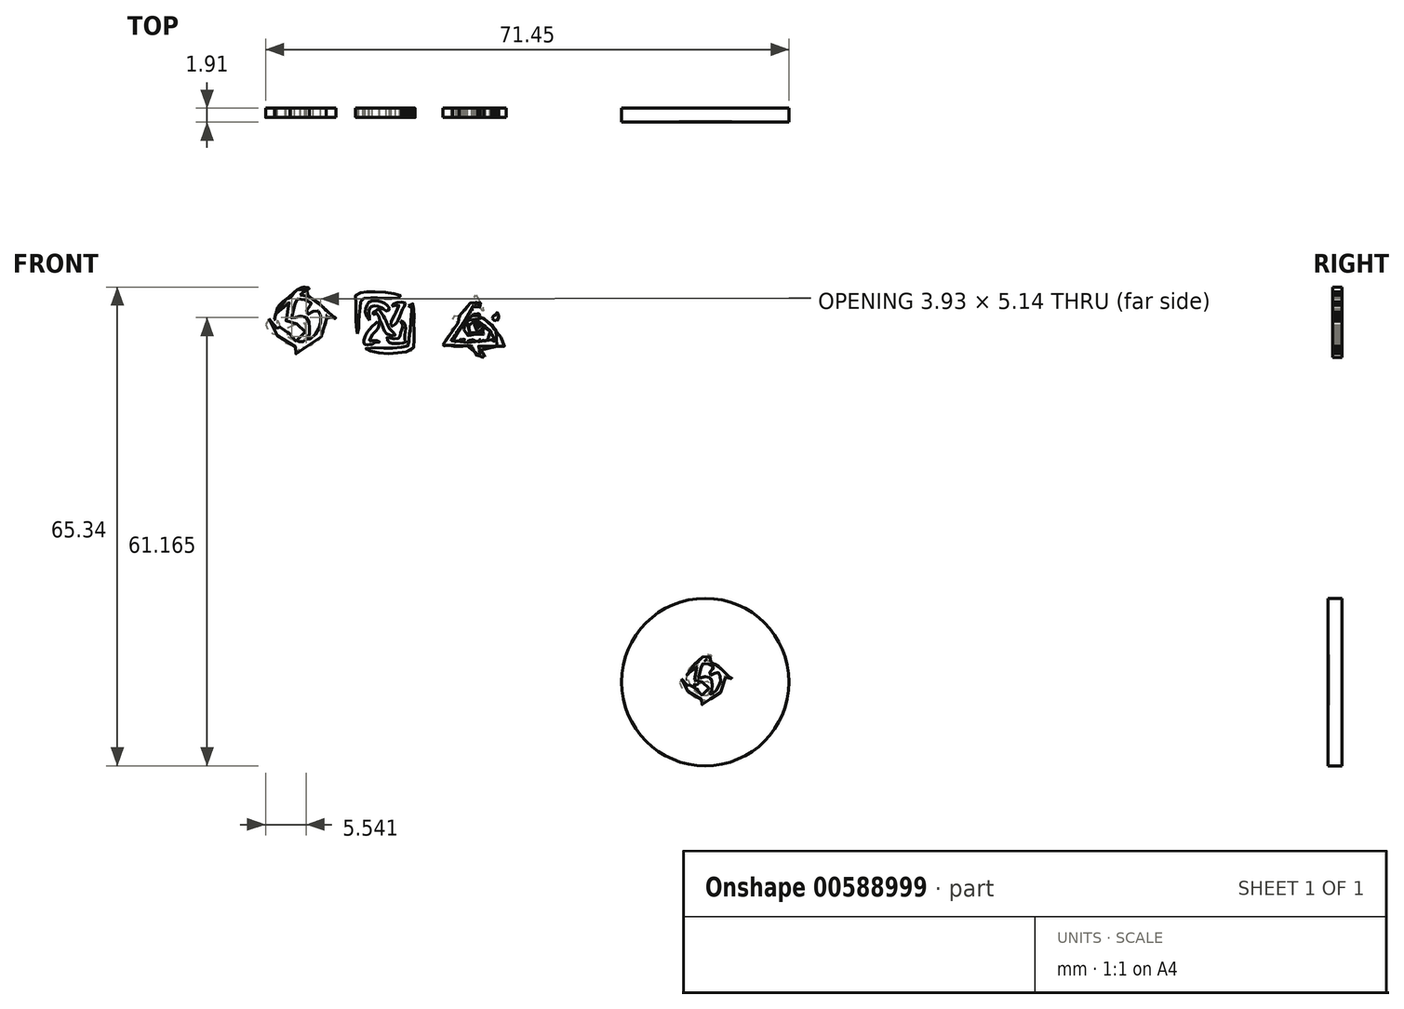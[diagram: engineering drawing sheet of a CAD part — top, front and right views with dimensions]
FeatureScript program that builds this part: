
annotation { "Feature Type Name" : "Feature", "Feature Type Description" : "" }
export const myFeature = defineFeature(function(context is Context, id is Id, definition is map)
    precondition{}
    {
        {
            var Q0;
            Q0=qCreatedBy(makeId("Front.planeOp"),FACE);
            var sketch = newSketch(context, id + "F0", { "sketchPlane" : qUnion([Q0])});
            skCircle(sketch, "E0", {"center": v(0, 0) * mm, "radius": 11.43 * mm});
            skSolve(sketch);
        }
        {
            var Q0;
            Q0=qSketchRegion(id+"F0",true);
            extrude(context, id + "F1", {"entities" : qUnion([Q0]), "depth" : 1.9 * mm, "offsetDistance" : 25.4 * mm});
        }
        {
            var Q0;
            Q0=makeQuery(id+"F1.opExtrude","CAP_FACE",FACE,{"disambiguationData":[OSD([sQuery(id+"F0.wireOp",EDGE,"E0")])],"isStart":false});
            var sketch = newSketch(context, id + "F2", { "sketchPlane" : qUnion([Q0])});
            skFitSpline(sketch, "E1", {"points": [v(-3.24, 0.45) * mm, v(-3.55, 0.04) * mm, v(-3.49, -0.19) * mm, v(-3.34, -0.6) * mm, v(-3.02, -0.9) * mm, v(-2.64, -1.13) * mm, v(-2.34, -1.25) * mm, v(-2.3, -1.13) * mm, v(-2.1, -1.5) * mm, v(-1.73, -1.77) * mm, v(-1.3, -2.12) * mm, v(-0.73, -2.32) * mm, v(-0.3, -2.43) * mm, v(0.02, -2.42) * mm, v(-0.07, -2.54) * mm, v(-0.16, -2.68) * mm, v(-0.32, -2.86) * mm, v(-0.45, -2.97) * mm, v(-0.58, -3.05) * mm, v(-0.6, -3.15) * mm, v(-0.45, -3.1) * mm, v(-0.28, -3.04) * mm, v(-0.18, -3) * mm, v(-0.02, -2.86) * mm, v(0.1, -2.77) * mm, v(0.18, -2.65) * mm, v(0.23, -2.56) * mm, v(0.3, -2.5) * mm, v(0.33, -2.4) * mm, v(0.53, -2.37) * mm, v(0.74, -2.32) * mm, v(0.97, -2.25) * mm, v(1.17, -2.16) * mm, v(1.39, -2) * mm, v(1.54, -1.9) * mm, v(1.75, -1.8) * mm, v(1.9, -1.64) * mm, v(2.05, -1.47) * mm, v(2.2, -1.23) * mm, v(2.35, -0.98) * mm, v(2.46, -0.8) * mm, v(2.57, -0.46) * mm, v(2.66, -0.14) * mm, v(2.72, 0.23) * mm, v(2.7, 0.55) * mm, v(2.65, 0.84) * mm, v(2.79, 0.76) * mm, v(2.98, 0.66) * mm, v(3.23, 0.55) * mm, v(3.44, 0.51) * mm, v(3.58, 0.52) * mm, v(3.6, 0.57) * mm, v(3.4, 0.67) * mm, v(3.26, 0.77) * mm, v(3.16, 0.89) * mm, v(3, 1) * mm, v(2.86, 1.12) * mm, v(2.76, 1.23) * mm, v(2.57, 1.37) * mm, v(2.48, 1.47) * mm, v(2.38, 1.63) * mm, v(2.21, 1.74) * mm, v(2.07, 1.9) * mm, v(1.87, 2.07) * mm, v(1.76, 2.2) * mm, v(1.56, 2.33) * mm, v(1.4, 2.41) * mm, v(1.15, 2.53) * mm, v(0.96, 2.72) * mm, v(0.66, 2.81) * mm, v(0.46, 2.81) * mm, v(0.16, 2.91) * mm, v(-0.02, 2.89) * mm, v(0.08, 3) * mm, v(0.16, 3.1) * mm, v(0.28, 3.18) * mm, v(0.5, 3.3) * mm, v(0.64, 3.4) * mm, v(0.84, 3.51) * mm, v(0.9, 3.6) * mm, v(0.62, 3.66) * mm, v(0.43, 3.7) * mm, v(0.26, 3.7) * mm, v(0.1, 3.65) * mm, v(-0.02, 3.59) * mm, v(-0.19, 3.52) * mm, v(-0.37, 3.38) * mm, v(-0.53, 3.25) * mm, v(-0.65, 3.12) * mm, v(-0.76, 2.97) * mm, v(-0.81, 2.87) * mm, v(-0.93, 2.7) * mm, v(-1.18, 2.6) * mm, v(-1.34, 2.52) * mm, v(-1.47, 2.45) * mm, v(-1.69, 2.3) * mm, v(-1.88, 2.16) * mm, v(-2.1, 1.93) * mm, v(-2.25, 1.75) * mm, v(-2.35, 1.5) * mm, v(-2.46, 1.26) * mm, v(-2.5, 1.02) * mm, v(-2.6, 0.77) * mm, v(-2.61, 0.53) * mm, v(-2.62, 0.36) * mm, v(-2.56, 0.33) * mm, v(-2.54, 0.55) * mm, v(-2.5, 0.7) * mm, v(-2.4, 0.9) * mm, v(-2.28, 1.15) * mm, v(-2.16, 1.33) * mm, v(-2.01, 1.56) * mm, v(-1.84, 1.8) * mm, v(-1.69, 1.92) * mm, v(-1.5, 2.05) * mm, v(-1.25, 2.22) * mm, v(-1.09, 2.31) * mm, v(-1.16, 2.12) * mm, v(-1.27, 1.86) * mm, v(-1.3, 1.73) * mm, v(-1.37, 1.39) * mm, v(-1.39, 1.23) * mm, v(-1.42, 0.93) * mm, v(-1.43, 0.69) * mm, v(-1.44, 0.4) * mm, v(-1.47, 0.07) * mm, v(-1.44, -0.2) * mm, v(-1.42, -0.5) * mm, v(-1.15, -0.34) * mm, v(-0.97, -0.26) * mm, v(-0.72, -0.18) * mm, v(-0.47, -0.08) * mm, v(-0.2, 0) * mm, v(0.1, 0.1) * mm, v(0.25, 0.13) * mm, v(0.38, 0.08) * mm, v(0.48, -0.18) * mm, v(0.48, -0.4) * mm, v(0.5, -0.6) * mm, v(0.5, -0.8) * mm, v(0.47, -1) * mm, v(0.46, -1.29) * mm, v(0.38, -1.62) * mm, v(0.33, -1.82) * mm, v(0.18, -1.88) * mm, v(-0.02, -1.87) * mm, v(-0.25, -1.83) * mm, v(-0.47, -1.8) * mm, v(-0.7, -1.75) * mm, v(-0.85, -1.65) * mm, v(-1.06, -1.52) * mm, v(-1.22, -1.44) * mm, v(-1.4, -1.3) * mm, v(-1.57, -1.1) * mm, v(-1.3, -1.1) * mm, v(-1.07, -1.05) * mm, v(-0.97, -1.04) * mm, v(-1.12, -0.92) * mm, v(-1.24, -0.85) * mm, v(-1.42, -0.8) * mm, v(-1.59, -0.77) * mm, v(-1.77, -0.74) * mm, v(-1.86, -0.74) * mm, v(-2, -0.53) * mm, v(-2.1, -0.3) * mm, v(-2.13, -0.1) * mm, v(-2.21, 0.12) * mm, v(-2.3, 0.26) * mm, v(-2.38, 0.33) * mm, v(-2.38, 0.06) * mm, v(-2.4, -0.06) * mm, v(-2.42, -0.25) * mm, v(-2.42, -0.4) * mm, v(-2.42, -0.59) * mm, v(-2.56, -0.53) * mm, v(-2.67, -0.42) * mm, v(-2.83, -0.27) * mm, v(-2.86, -0.14) * mm, v(-2.93, 0.09) * mm, v(-2.98, 0.3) * mm, v(-3.1, 0.43) * mm, v(-3.24, 0.45) * mm]});
            skFitSpline(sketch, "E2", {"points": [v(-0.32, 2.52) * mm, v(0.04, 2.5) * mm, v(0.43, 2.43) * mm, v(0.8, 2.33) * mm, v(1, 2.17) * mm, v(1.28, 1.96) * mm, v(1.13, 1.9) * mm, v(0.97, 1.78) * mm, v(0.78, 1.64) * mm, v(0.62, 1.46) * mm, v(0.62, 1.25) * mm, v(0.64, 1.08) * mm, v(0.63, 0.94) * mm, v(0.89, 0.97) * mm, v(1.04, 1.1) * mm, v(1.19, 1.16) * mm, v(1.37, 1.27) * mm, v(1.55, 1.3) * mm, v(1.72, 1.3) * mm, v(1.87, 1.25) * mm, v(1.97, 1.06) * mm, v(2.04, 0.88) * mm, v(2.06, 0.6) * mm, v(2.07, 0.2) * mm, v(2.07, -0.04) * mm, v(1.97, -0.28) * mm, v(1.84, -0.58) * mm, v(1.78, -0.8) * mm, v(1.63, -0.98) * mm, v(1.46, -1.2) * mm, v(1.24, -1.4) * mm, v(0.95, -1.6) * mm, v(0.72, -1.72) * mm, v(0.63, -1.74) * mm, v(0.74, -1.55) * mm, v(0.82, -1.35) * mm, v(0.9, -1.15) * mm, v(0.9, -0.89) * mm, v(0.93, -0.62) * mm, v(0.93, -0.38) * mm, v(0.91, -0.17) * mm, v(0.91, 0.04) * mm, v(0.87, 0.24) * mm, v(0.78, 0.41) * mm, v(0.62, 0.58) * mm, v(0.42, 0.7) * mm, v(0.26, 0.7) * mm, v(0.04, 0.74) * mm, v(-0.1, 0.7) * mm, v(-0.33, 0.66) * mm, v(-0.53, 0.59) * mm, v(-0.76, 0.51) * mm, v(-0.94, 0.43) * mm, v(-0.88, 0.62) * mm, v(-0.87, 0.8) * mm, v(-0.76, 1.27) * mm, v(-0.66, 1.73) * mm, v(-0.6, 1.89) * mm, v(-0.5, 2.14) * mm, v(-0.41, 2.32) * mm, v(-0.32, 2.52) * mm]});
            skLineSegment(sketch, "E3", {"start": v(0.1, 0.4) * mm, "end": v(0.1, 8.03) * mm, "construction": true});
            skLineSegment(sketch, "E4", {"start": v(-4.62, 3.36) * mm, "end": v(3.83, 3.36) * mm, "construction": true});
            skSolve(sketch);
        }
        {
            var Q0;
            Q0=qSketchRegion(id+"F2",true);
            extrude(context, id + "F3", {"entities" : qUnion([Q0]), "operationType" : NewBodyOperationType.REMOVE, "oppositeDirection" : true, "depth" : 0.13 * mm, "offsetDistance" : 25.4 * mm});
        }
        {
            var Q0;
            Q0=qCreatedBy(makeId("Front.planeOp"),FACE);
            var sketch = newSketch(context, id + "F4", { "sketchPlane" : qUnion([Q0])});
            skFitSpline(sketch, "E5", {"points": [v(-59.6, 49.55) * mm, v(-60.01, 49) * mm, v(-59.93, 48.7) * mm, v(-59.74, 48.15) * mm, v(-59.3, 47.74) * mm, v(-58.8, 47.43) * mm, v(-58.4, 47.27) * mm, v(-58.35, 47.43) * mm, v(-58.06, 46.95) * mm, v(-57.58, 46.58) * mm, v(-57, 46.1) * mm, v(-56.25, 45.85) * mm, v(-55.67, 45.7) * mm, v(-55.25, 45.71) * mm, v(-55.36, 45.55) * mm, v(-55.49, 45.36) * mm, v(-55.7, 45.12) * mm, v(-55.87, 44.98) * mm, v(-56.05, 44.86) * mm, v(-56.07, 44.73) * mm, v(-55.87, 44.8) * mm, v(-55.65, 44.88) * mm, v(-55.5, 44.94) * mm, v(-55.3, 45.12) * mm, v(-55.14, 45.25) * mm, v(-55.02, 45.4) * mm, v(-54.96, 45.52) * mm, v(-54.88, 45.62) * mm, v(-54.83, 45.73) * mm, v(-54.56, 45.78) * mm, v(-54.28, 45.84) * mm, v(-53.98, 45.94) * mm, v(-53.7, 46.06) * mm, v(-53.42, 46.27) * mm, v(-53.2, 46.4) * mm, v(-52.94, 46.54) * mm, v(-52.73, 46.75) * mm, v(-52.53, 46.98) * mm, v(-52.33, 47.3) * mm, v(-52.13, 47.64) * mm, v(-51.99, 47.86) * mm, v(-51.83, 48.33) * mm, v(-51.72, 48.76) * mm, v(-51.64, 49.25) * mm, v(-51.67, 49.68) * mm, v(-51.74, 50.07) * mm, v(-51.54, 49.96) * mm, v(-51.28, 49.83) * mm, v(-50.95, 49.68) * mm, v(-50.67, 49.63) * mm, v(-50.48, 49.65) * mm, v(-50.45, 49.71) * mm, v(-50.74, 49.84) * mm, v(-50.92, 49.97) * mm, v(-51.04, 50.13) * mm, v(-51.27, 50.3) * mm, v(-51.45, 50.44) * mm, v(-51.58, 50.58) * mm, v(-51.83, 50.78) * mm, v(-51.96, 50.9) * mm, v(-52.1, 51.12) * mm, v(-52.32, 51.26) * mm, v(-52.5, 51.47) * mm, v(-52.77, 51.72) * mm, v(-52.91, 51.88) * mm, v(-53.19, 52.06) * mm, v(-53.41, 52.17) * mm, v(-53.73, 52.33) * mm, v(-53.99, 52.57) * mm, v(-54.4, 52.7) * mm, v(-54.65, 52.7) * mm, v(-55.05, 52.84) * mm, v(-55.3, 52.8) * mm, v(-55.16, 52.95) * mm, v(-55.05, 53.1) * mm, v(-54.9, 53.19) * mm, v(-54.6, 53.37) * mm, v(-54.4, 53.5) * mm, v(-54.15, 53.64) * mm, v(-54.07, 53.75) * mm, v(-54.44, 53.83) * mm, v(-54.7, 53.9) * mm, v(-54.92, 53.9) * mm, v(-55.13, 53.82) * mm, v(-55.3, 53.74) * mm, v(-55.52, 53.64) * mm, v(-55.76, 53.47) * mm, v(-55.98, 53.3) * mm, v(-56.14, 53.11) * mm, v(-56.29, 52.92) * mm, v(-56.35, 52.78) * mm, v(-56.51, 52.55) * mm, v(-56.85, 52.4) * mm, v(-57.06, 52.31) * mm, v(-57.24, 52.21) * mm, v(-57.53, 52.02) * mm, v(-57.78, 51.83) * mm, v(-58.09, 51.52) * mm, v(-58.28, 51.28) * mm, v(-58.4, 50.95) * mm, v(-58.55, 50.62) * mm, v(-58.62, 50.3) * mm, v(-58.74, 49.98) * mm, v(-58.76, 49.66) * mm, v(-58.78, 49.43) * mm, v(-58.7, 49.38) * mm, v(-58.66, 49.67) * mm, v(-58.6, 49.88) * mm, v(-58.49, 50.14) * mm, v(-58.31, 50.48) * mm, v(-58.15, 50.72) * mm, v(-57.96, 51.02) * mm, v(-57.73, 51.35) * mm, v(-57.52, 51.5) * mm, v(-57.27, 51.68) * mm, v(-56.95, 51.9) * mm, v(-56.72, 52.04) * mm, v(-56.82, 51.78) * mm, v(-56.96, 51.42) * mm, v(-57, 51.26) * mm, v(-57.1, 50.8) * mm, v(-57.12, 50.59) * mm, v(-57.17, 50.18) * mm, v(-57.18, 49.86) * mm, v(-57.2, 49.5) * mm, v(-57.23, 49.04) * mm, v(-57.2, 48.67) * mm, v(-57.17, 48.28) * mm, v(-56.81, 48.5) * mm, v(-56.57, 48.6) * mm, v(-56.23, 48.7) * mm, v(-55.9, 48.84) * mm, v(-55.54, 48.94) * mm, v(-55.13, 49.07) * mm, v(-54.93, 49.11) * mm, v(-54.76, 49.05) * mm, v(-54.63, 48.7) * mm, v(-54.63, 48.4) * mm, v(-54.6, 48.15) * mm, v(-54.6, 47.87) * mm, v(-54.64, 47.61) * mm, v(-54.66, 47.23) * mm, v(-54.77, 46.78) * mm, v(-54.83, 46.52) * mm, v(-55.02, 46.44) * mm, v(-55.3, 46.44) * mm, v(-55.6, 46.5) * mm, v(-55.9, 46.54) * mm, v(-56.21, 46.6) * mm, v(-56.4, 46.73) * mm, v(-56.68, 46.91) * mm, v(-56.9, 47.03) * mm, v(-57.13, 47.22) * mm, v(-57.37, 47.46) * mm, v(-57.02, 47.48) * mm, v(-56.7, 47.54) * mm, v(-56.57, 47.56) * mm, v(-56.76, 47.72) * mm, v(-56.92, 47.81) * mm, v(-57.17, 47.88) * mm, v(-57.4, 47.91) * mm, v(-57.63, 47.96) * mm, v(-57.76, 47.96) * mm, v(-57.94, 48.24) * mm, v(-58.07, 48.54) * mm, v(-58.12, 48.8) * mm, v(-58.23, 49.1) * mm, v(-58.36, 49.29) * mm, v(-58.45, 49.38) * mm, v(-58.45, 49.03) * mm, v(-58.49, 48.87) * mm, v(-58.5, 48.6) * mm, v(-58.5, 48.4) * mm, v(-58.5, 48.16) * mm, v(-58.7, 48.24) * mm, v(-58.84, 48.39) * mm, v(-59.05, 48.58) * mm, v(-59.1, 48.76) * mm, v(-59.2, 49.06) * mm, v(-59.26, 49.35) * mm, v(-59.42, 49.52) * mm, v(-59.6, 49.55) * mm]});
            skFitSpline(sketch, "E6", {"points": [v(-55.7, 52.3) * mm, v(-55.21, 52.29) * mm, v(-54.7, 52.2) * mm, v(-54.21, 52.06) * mm, v(-53.92, 51.85) * mm, v(-53.55, 51.56) * mm, v(-53.76, 51.48) * mm, v(-53.97, 51.32) * mm, v(-54.23, 51.14) * mm, v(-54.44, 50.9) * mm, v(-54.44, 50.61) * mm, v(-54.42, 50.38) * mm, v(-54.39, 50.2) * mm, v(-54.08, 50.24) * mm, v(-53.87, 50.41) * mm, v(-53.68, 50.5) * mm, v(-53.44, 50.64) * mm, v(-53.2, 50.67) * mm, v(-52.97, 50.67) * mm, v(-52.77, 50.62) * mm, v(-52.64, 50.36) * mm, v(-52.54, 50.12) * mm, v(-52.52, 49.73) * mm, v(-52.5, 49.22) * mm, v(-52.5, 48.9) * mm, v(-52.63, 48.57) * mm, v(-52.8, 48.17) * mm, v(-52.89, 47.88) * mm, v(-53.1, 47.64) * mm, v(-53.32, 47.34) * mm, v(-53.61, 47.08) * mm, v(-54, 46.8) * mm, v(-54.3, 46.65) * mm, v(-54.43, 46.61) * mm, v(-54.29, 46.87) * mm, v(-54.17, 47.14) * mm, v(-54.08, 47.4) * mm, v(-54.06, 47.76) * mm, v(-54.03, 48.11) * mm, v(-54.03, 48.43) * mm, v(-54.05, 48.72) * mm, v(-54.05, 49) * mm, v(-54.11, 49.27) * mm, v(-54.23, 49.5) * mm, v(-54.44, 49.72) * mm, v(-54.7, 49.87) * mm, v(-54.92, 49.89) * mm, v(-55.22, 49.94) * mm, v(-55.42, 49.89) * mm, v(-55.7, 49.82) * mm, v(-55.98, 49.73) * mm, v(-56.29, 49.63) * mm, v(-56.52, 49.52) * mm, v(-56.44, 49.78) * mm, v(-56.43, 50.02) * mm, v(-56.29, 50.65) * mm, v(-56.16, 51.26) * mm, v(-56.06, 51.47) * mm, v(-55.93, 51.8) * mm, v(-55.82, 52.05) * mm, v(-55.7, 52.3) * mm]});
            skPoint(sketch, "E7", {"position": v(-55.42, 49.44) * mm});
            skLineSegment(sketch, "E8", {"start": v(-55.42, 46.77) * mm, "end": v(-55.42, 54.4) * mm, "construction": true});
            skFitSpline(sketch, "E9", {"points": [v(-47.52, 47.56) * mm, v(-47.63, 48.1) * mm, v(-47.64, 48.43) * mm, v(-47.7, 48.92) * mm, v(-47.67, 49.4) * mm, v(-47.7, 50.15) * mm, v(-47.67, 50.53) * mm, v(-47.65, 51.1) * mm, v(-47.68, 51.78) * mm, v(-47.69, 52.58) * mm, v(-47.7, 52.98) * mm, v(-47.2, 53.05) * mm, v(-46.9, 53.16) * mm, v(-46.5, 53.23) * mm, v(-45.99, 53.26) * mm, v(-45.36, 53.27) * mm, v(-44.37, 53.25) * mm, v(-43.35, 53.18) * mm, v(-42.55, 53.04) * mm, v(-42.11, 52.94) * mm, v(-41.71, 52.78) * mm, v(-41.47, 52.63) * mm, v(-41.6, 52.49) * mm, v(-41.9, 52.43) * mm, v(-42.18, 52.38) * mm, v(-42.58, 52.34) * mm, v(-43.24, 52.37) * mm, v(-43.77, 52.36) * mm, v(-44.2, 52.4) * mm, v(-44.7, 52.41) * mm, v(-45.01, 52.4) * mm, v(-45.5, 52.4) * mm, v(-46.1, 52.44) * mm, v(-46.53, 52.37) * mm, v(-46.72, 52.33) * mm, v(-46.94, 52.23) * mm, v(-47.04, 51.94) * mm, v(-47.08, 51.62) * mm, v(-47.11, 51.24) * mm, v(-47.16, 50.75) * mm, v(-47.2, 50.22) * mm, v(-47.3, 49.71) * mm, v(-47.33, 49.33) * mm, v(-47.35, 48.98) * mm, v(-47.36, 48.66) * mm, v(-47.33, 48.13) * mm, v(-47.4, 47.8) * mm, v(-47.52, 47.56) * mm]});
            skFitSpline(sketch, "E10", {"points": [v(-45.33, 50.17) * mm, v(-45.47, 50.36) * mm, v(-45.28, 50.45) * mm, v(-45.01, 50.55) * mm, v(-44.9, 50.74) * mm, v(-44.7, 50.89) * mm, v(-44.55, 50.93) * mm, v(-44.41, 50.62) * mm, v(-44.26, 50.4) * mm, v(-44.15, 50.16) * mm, v(-43.92, 49.89) * mm, v(-43.79, 49.76) * mm, v(-43.7, 49.55) * mm, v(-43.6, 49.3) * mm, v(-43.47, 48.98) * mm, v(-43.3, 48.6) * mm, v(-43.09, 48.2) * mm, v(-42.84, 47.98) * mm, v(-42.61, 47.8) * mm, v(-42.41, 47.57) * mm, v(-42.27, 47.44) * mm, v(-42.43, 47.3) * mm, v(-42.63, 47.25) * mm, v(-42.78, 47.28) * mm, v(-43, 47.3) * mm, v(-43.28, 47.43) * mm, v(-43.52, 47.55) * mm, v(-43.76, 47.83) * mm, v(-43.93, 48.24) * mm, v(-44.1, 48.6) * mm, v(-44.3, 49.08) * mm, v(-44.44, 49.49) * mm, v(-44.53, 49.83) * mm, v(-44.76, 50.3) * mm, v(-45, 50.28) * mm, v(-45.33, 50.17) * mm]});
            skFitSpline(sketch, "E11", {"points": [v(-45.86, 49.4) * mm, v(-46.07, 49.7) * mm, v(-46.27, 49.98) * mm, v(-46.3, 50.16) * mm, v(-46.38, 50.4) * mm, v(-46.4, 50.74) * mm, v(-46.31, 51.2) * mm, v(-46.1, 51.6) * mm, v(-45.88, 51.91) * mm, v(-45.36, 52.03) * mm, v(-44.83, 52.06) * mm, v(-44.4, 51.94) * mm, v(-43.9, 51.76) * mm, v(-43.5, 51.47) * mm, v(-43.23, 51.18) * mm, v(-43.1, 50.98) * mm, v(-43.28, 50.73) * mm, v(-43.4, 50.57) * mm, v(-43.69, 50.71) * mm, v(-43.94, 50.9) * mm, v(-44.15, 51.04) * mm, v(-44.42, 51.2) * mm, v(-44.81, 51.29) * mm, v(-45.2, 51.33) * mm, v(-45.63, 51.2) * mm, v(-45.86, 50.9) * mm, v(-45.96, 50.54) * mm, v(-45.89, 50.16) * mm, v(-45.86, 49.77) * mm, v(-45.86, 49.4) * mm]});
            skFitSpline(sketch, "E12", {"points": [v(-42.83, 51.26) * mm, v(-42.81, 51.48) * mm, v(-42.55, 51.59) * mm, v(-42.29, 51.72) * mm, v(-41.89, 51.78) * mm, v(-41.52, 51.86) * mm, v(-41.07, 51.91) * mm, v(-40.96, 51.73) * mm, v(-41.05, 51.47) * mm, v(-41.07, 51.26) * mm, v(-41.22, 51.1) * mm, v(-41.34, 50.87) * mm, v(-41.43, 50.53) * mm, v(-41.6, 50.26) * mm, v(-41.7, 50) * mm, v(-41.8, 49.71) * mm, v(-41.9, 49.49) * mm, v(-42, 49.29) * mm, v(-42.1, 49.12) * mm, v(-42.15, 48.98) * mm, v(-42.24, 48.86) * mm, v(-42.4, 48.82) * mm, v(-42.58, 48.7) * mm, v(-42.75, 48.54) * mm, v(-42.85, 48.6) * mm, v(-42.9, 48.72) * mm, v(-42.92, 48.88) * mm, v(-42.92, 49.05) * mm, v(-42.88, 49.21) * mm, v(-42.78, 49.39) * mm, v(-42.64, 49.62) * mm, v(-42.56, 49.84) * mm, v(-42.44, 50.07) * mm, v(-42.35, 50.3) * mm, v(-42.25, 50.48) * mm, v(-42.13, 50.7) * mm, v(-42.02, 50.93) * mm, v(-42, 51.06) * mm, v(-41.98, 51.18) * mm, v(-41.89, 51.24) * mm, v(-41.8, 51.3) * mm, v(-41.73, 51.36) * mm, v(-41.82, 51.37) * mm, v(-41.9, 51.4) * mm, v(-42, 51.41) * mm, v(-42.23, 51.43) * mm, v(-42.44, 51.4) * mm, v(-42.56, 51.37) * mm, v(-42.72, 51.35) * mm, v(-42.78, 51.32) * mm, v(-42.83, 51.26) * mm]});
            skFitSpline(sketch, "E13", {"points": [v(-40.51, 51.34) * mm, v(-40.38, 51.4) * mm, v(-40.25, 51.43) * mm, v(-40.15, 51.44) * mm, v(-40.15, 51.57) * mm, v(-40.17, 51.73) * mm, v(-40.17, 51.8) * mm, v(-40.07, 51.73) * mm, v(-39.95, 51.65) * mm, v(-39.88, 51.54) * mm, v(-39.79, 51.46) * mm, v(-39.79, 51.37) * mm, v(-39.8, 51.24) * mm, v(-39.73, 51.17) * mm, v(-39.81, 51.05) * mm, v(-39.8, 50.93) * mm, v(-39.73, 50.85) * mm, v(-39.82, 50.83) * mm, v(-39.85, 50.75) * mm, v(-39.79, 50.71) * mm, v(-39.79, 50.6) * mm, v(-39.73, 50.54) * mm, v(-39.74, 50.43) * mm, v(-39.81, 50.29) * mm, v(-39.77, 50.16) * mm, v(-39.79, 49.98) * mm, v(-39.77, 49.8) * mm, v(-39.77, 49.7) * mm, v(-39.78, 49.57) * mm, v(-39.78, 49.5) * mm, v(-39.7, 49.43) * mm, v(-39.6, 49.37) * mm, v(-39.65, 49.3) * mm, v(-39.73, 49.27) * mm, v(-39.78, 49.08) * mm, v(-39.78, 48.84) * mm, v(-39.79, 48.67) * mm, v(-39.71, 48.6) * mm, v(-39.77, 48.43) * mm, v(-39.74, 48.25) * mm, v(-39.72, 48.13) * mm, v(-39.76, 47.96) * mm, v(-39.8, 47.78) * mm, v(-39.83, 47.6) * mm, v(-39.82, 47.44) * mm, v(-39.82, 47.31) * mm, v(-39.84, 47.13) * mm, v(-39.83, 47.02) * mm, v(-39.82, 46.85) * mm, v(-39.73, 46.8) * mm, v(-39.73, 46.63) * mm, v(-39.74, 46.47) * mm, v(-39.78, 46.33) * mm, v(-39.82, 46.24) * mm, v(-39.82, 46.06) * mm, v(-39.82, 45.8) * mm, v(-39.82, 45.58) * mm, v(-39.83, 45.33) * mm, v(-39.91, 45.2) * mm, v(-40.14, 45.16) * mm, v(-40.35, 45.14) * mm, v(-40.59, 45.12) * mm, v(-40.78, 45.1) * mm, v(-40.9, 45.08) * mm, v(-41.04, 45.02) * mm, v(-41.21, 45.02) * mm, v(-41.4, 45) * mm, v(-41.56, 44.98) * mm, v(-41.73, 44.95) * mm, v(-41.92, 44.94) * mm, v(-42.1, 44.93) * mm, v(-42.26, 44.88) * mm, v(-42.39, 44.85) * mm, v(-42.6, 44.84) * mm, v(-42.87, 44.85) * mm, v(-43.06, 44.83) * mm, v(-43.26, 44.84) * mm, v(-43.45, 44.84) * mm, v(-43.63, 44.85) * mm, v(-43.87, 44.87) * mm, v(-44.06, 44.88) * mm, v(-44.25, 44.9) * mm, v(-44.48, 44.91) * mm, v(-44.65, 44.93) * mm, v(-44.86, 44.93) * mm, v(-45.03, 44.96) * mm, v(-45.23, 44.99) * mm, v(-45.4, 45.04) * mm, v(-45.54, 45.08) * mm, v(-45.68, 45.14) * mm, v(-45.78, 45.19) * mm, v(-45.97, 45.24) * mm, v(-46.12, 45.28) * mm, v(-46.21, 45.32) * mm, v(-46.24, 45.4) * mm, v(-46.27, 45.44) * mm, v(-46.3, 45.4) * mm, v(-46.36, 45.4) * mm, v(-46.4, 45.44) * mm, v(-46.35, 45.5) * mm, v(-46.3, 45.54) * mm, v(-46.17, 45.6) * mm, v(-46.04, 45.63) * mm, v(-45.87, 45.65) * mm, v(-45.63, 45.65) * mm, v(-45.47, 45.65) * mm, v(-45.26, 45.64) * mm, v(-44.98, 45.64) * mm, v(-44.82, 45.63) * mm, v(-44.67, 45.63) * mm, v(-44.45, 45.62) * mm, v(-44.3, 45.64) * mm, v(-44.15, 45.64) * mm, v(-43.93, 45.63) * mm, v(-43.87, 45.56) * mm, v(-43.65, 45.55) * mm, v(-43.5, 45.56) * mm, v(-43.3, 45.57) * mm, v(-43.08, 45.57) * mm, v(-42.83, 45.58) * mm, v(-42.73, 45.58) * mm, v(-42.54, 45.6) * mm, v(-42.36, 45.6) * mm, v(-42.2, 45.6) * mm, v(-42.04, 45.62) * mm, v(-41.92, 45.65) * mm, v(-41.75, 45.68) * mm, v(-41.58, 45.7) * mm, v(-41.42, 45.7) * mm, v(-41.26, 45.7) * mm, v(-41.1, 45.72) * mm, v(-40.96, 45.73) * mm, v(-40.87, 45.74) * mm, v(-40.82, 45.74) * mm, v(-40.67, 45.78) * mm, v(-40.58, 45.78) * mm, v(-40.56, 45.86) * mm, v(-40.56, 45.92) * mm, v(-40.55, 46.03) * mm, v(-40.55, 46.1) * mm, v(-40.54, 46.18) * mm, v(-40.54, 46.27) * mm, v(-40.51, 46.35) * mm, v(-40.46, 46.41) * mm, v(-40.44, 46.58) * mm, v(-40.43, 46.75) * mm, v(-40.44, 46.98) * mm, v(-40.37, 47.3) * mm, v(-40.38, 47.49) * mm, v(-40.29, 47.77) * mm, v(-40.25, 47.98) * mm, v(-40.25, 48.2) * mm, v(-40.24, 48.49) * mm, v(-40.22, 48.74) * mm, v(-40.22, 48.9) * mm, v(-40.19, 49.1) * mm, v(-40.18, 49.36) * mm, v(-40.16, 49.61) * mm, v(-40.11, 49.86) * mm, v(-40.1, 50.16) * mm, v(-40.08, 50.39) * mm, v(-40.03, 50.6) * mm, v(-40.04, 50.69) * mm, v(-40.05, 50.85) * mm, v(-40.05, 51.06) * mm, v(-40.02, 51.17) * mm, v(-39.98, 51.26) * mm, v(-40.02, 51.34) * mm, v(-40.08, 51.34) * mm, v(-40.14, 51.3) * mm, v(-40.22, 51.28) * mm, v(-40.28, 51.3) * mm, v(-40.37, 51.3) * mm, v(-40.41, 51.3) * mm, v(-40.51, 51.34) * mm]});
            skFitSpline(sketch, "E14", {"points": [v(-41.63, 49.32) * mm, v(-41.52, 49.33) * mm, v(-41.44, 49.31) * mm, v(-41.34, 49.26) * mm, v(-41.26, 49.18) * mm, v(-41.18, 49.13) * mm, v(-41.13, 49.07) * mm, v(-41.03, 48.96) * mm, v(-40.96, 48.86) * mm, v(-40.96, 48.69) * mm, v(-40.96, 48.46) * mm, v(-40.96, 48.36) * mm, v(-40.85, 48.35) * mm, v(-40.87, 48.29) * mm, v(-40.96, 48.25) * mm, v(-40.96, 48.14) * mm, v(-40.96, 48) * mm, v(-40.96, 47.78) * mm, v(-40.96, 47.7) * mm, v(-41.02, 47.7) * mm, v(-41.03, 47.6) * mm, v(-41.03, 47.44) * mm, v(-41.04, 47.3) * mm, v(-40.96, 47.3) * mm, v(-40.96, 47.13) * mm, v(-41.03, 47.04) * mm, v(-41.01, 46.9) * mm, v(-40.98, 46.73) * mm, v(-40.96, 46.65) * mm, v(-40.96, 46.54) * mm, v(-40.96, 46.43) * mm, v(-40.95, 46.35) * mm, v(-40.95, 46.3) * mm, v(-40.93, 46.27) * mm, v(-41.03, 46.26) * mm, v(-41.16, 46.25) * mm, v(-41.35, 46.23) * mm, v(-41.42, 46.23) * mm, v(-41.45, 46.23) * mm, v(-41.55, 46.22) * mm, v(-41.6, 46.22) * mm, v(-41.73, 46.22) * mm, v(-41.84, 46.2) * mm, v(-41.97, 46.22) * mm, v(-42.13, 46.21) * mm, v(-42.28, 46.2) * mm, v(-42.31, 46.2) * mm, v(-42.44, 46.2) * mm, v(-42.6, 46.2) * mm, v(-42.72, 46.2) * mm, v(-42.79, 46.21) * mm, v(-42.87, 46.23) * mm, v(-42.92, 46.26) * mm, v(-42.94, 46.3) * mm, v(-43, 46.3) * mm, v(-43.06, 46.32) * mm, v(-43.13, 46.32) * mm, v(-43.21, 46.37) * mm, v(-43.28, 46.42) * mm, v(-43.3, 46.5) * mm, v(-43.36, 46.58) * mm, v(-43.44, 46.66) * mm, v(-43.51, 46.75) * mm, v(-43.56, 46.83) * mm, v(-43.55, 46.93) * mm, v(-43.5, 46.98) * mm, v(-43.38, 47.04) * mm, v(-43.3, 47.06) * mm, v(-43.22, 47.04) * mm, v(-43.09, 47) * mm, v(-42.93, 46.97) * mm, v(-42.82, 46.96) * mm, v(-42.71, 46.94) * mm, v(-42.55, 46.89) * mm, v(-42.45, 46.87) * mm, v(-42.26, 46.86) * mm, v(-42.2, 46.86) * mm, v(-42.08, 46.87) * mm, v(-41.96, 46.89) * mm, v(-41.87, 46.93) * mm, v(-41.79, 46.95) * mm, v(-41.71, 46.98) * mm, v(-41.68, 47.1) * mm, v(-41.67, 47.18) * mm, v(-41.65, 47.3) * mm, v(-41.63, 47.43) * mm, v(-41.63, 47.52) * mm, v(-41.58, 47.63) * mm, v(-41.55, 47.73) * mm, v(-41.5, 47.8) * mm, v(-41.47, 47.9) * mm, v(-41.43, 48) * mm, v(-41.43, 48.13) * mm, v(-41.38, 48.24) * mm, v(-41.37, 48.35) * mm, v(-41.32, 48.48) * mm, v(-41.28, 48.55) * mm, v(-41.28, 48.66) * mm, v(-41.28, 48.77) * mm, v(-41.3, 48.85) * mm, v(-41.33, 48.88) * mm, v(-41.34, 48.96) * mm, v(-41.4, 49.02) * mm, v(-41.45, 49.06) * mm, v(-41.51, 49.13) * mm, v(-41.56, 49.17) * mm, v(-41.65, 49.25) * mm, v(-41.63, 49.32) * mm]});
            skFitSpline(sketch, "E15", {"points": [v(-44.75, 49.22) * mm, v(-44.8, 49.1) * mm, v(-44.88, 49.04) * mm, v(-44.93, 48.97) * mm, v(-45, 48.92) * mm, v(-45.13, 48.88) * mm, v(-45.25, 48.8) * mm, v(-45.31, 48.74) * mm, v(-45.38, 48.61) * mm, v(-45.45, 48.56) * mm, v(-45.55, 48.44) * mm, v(-45.6, 48.35) * mm, v(-45.7, 48.26) * mm, v(-45.78, 48.16) * mm, v(-45.84, 48.07) * mm, v(-45.89, 48) * mm, v(-45.98, 47.89) * mm, v(-46.04, 47.83) * mm, v(-46.12, 47.75) * mm, v(-46.2, 47.61) * mm, v(-46.26, 47.45) * mm, v(-46.36, 47.33) * mm, v(-46.42, 47.22) * mm, v(-46.5, 47.15) * mm, v(-46.56, 47.03) * mm, v(-46.61, 46.86) * mm, v(-46.6, 46.7) * mm, v(-46.64, 46.64) * mm, v(-46.7, 46.56) * mm, v(-46.73, 46.46) * mm, v(-46.72, 46.35) * mm, v(-46.66, 46.3) * mm, v(-46.6, 46.3) * mm, v(-46.64, 46.15) * mm, v(-46.69, 46.07) * mm, v(-46.61, 46.04) * mm, v(-46.55, 46.1) * mm, v(-46.5, 46.09) * mm, v(-46.44, 46.06) * mm, v(-46.35, 46.13) * mm, v(-46.29, 46.12) * mm, v(-46.25, 46.08) * mm, v(-46.16, 46.02) * mm, v(-46.1, 46) * mm, v(-46.05, 46.07) * mm, v(-45.99, 46.1) * mm, v(-45.95, 46.07) * mm, v(-45.9, 46.04) * mm, v(-45.83, 46.1) * mm, v(-45.75, 46.12) * mm, v(-45.65, 46.15) * mm, v(-45.62, 46.2) * mm, v(-45.53, 46.2) * mm, v(-45.48, 46.14) * mm, v(-45.45, 46.1) * mm, v(-45.44, 46.17) * mm, v(-45.42, 46.22) * mm, v(-45.39, 46.22) * mm, v(-45.27, 46.3) * mm, v(-45.2, 46.3) * mm, v(-45.05, 46.3) * mm, v(-44.99, 46.3) * mm, v(-44.96, 46.35) * mm, v(-44.93, 46.38) * mm, v(-44.88, 46.38) * mm, v(-44.85, 46.36) * mm, v(-44.83, 46.37) * mm, v(-44.69, 46.38) * mm, v(-44.62, 46.37) * mm, v(-44.56, 46.35) * mm, v(-44.5, 46.35) * mm, v(-44.45, 46.38) * mm, v(-44.48, 46.42) * mm, v(-44.54, 46.46) * mm, v(-44.59, 46.5) * mm, v(-44.62, 46.54) * mm, v(-44.7, 46.58) * mm, v(-44.78, 46.6) * mm, v(-44.85, 46.59) * mm, v(-44.92, 46.61) * mm, v(-45, 46.6) * mm, v(-45.14, 46.6) * mm, v(-45.23, 46.6) * mm, v(-45.32, 46.6) * mm, v(-45.44, 46.6) * mm, v(-45.53, 46.6) * mm, v(-45.7, 46.61) * mm, v(-45.81, 46.61) * mm, v(-45.84, 46.62) * mm, v(-45.84, 46.71) * mm, v(-45.82, 46.76) * mm, v(-45.77, 46.83) * mm, v(-45.72, 46.94) * mm, v(-45.66, 47.06) * mm, v(-45.6, 47.14) * mm, v(-45.54, 47.23) * mm, v(-45.5, 47.3) * mm, v(-45.43, 47.38) * mm, v(-45.34, 47.5) * mm, v(-45.29, 47.58) * mm, v(-45.22, 47.67) * mm, v(-45.14, 47.76) * mm, v(-45.06, 47.82) * mm, v(-44.96, 47.97) * mm, v(-44.9, 48.03) * mm, v(-44.77, 48.17) * mm, v(-44.7, 48.25) * mm, v(-44.64, 48.35) * mm, v(-44.6, 48.5) * mm, v(-44.56, 48.62) * mm, v(-44.52, 48.74) * mm, v(-44.52, 48.95) * mm, v(-44.54, 49.04) * mm, v(-44.57, 49.08) * mm, v(-44.63, 49.15) * mm, v(-44.7, 49.19) * mm, v(-44.75, 49.22) * mm]});
            skLineSegment(sketch, "E16", {"start": v(-43.9, 44.06) * mm, "end": v(-43.77, 53.85) * mm, "construction": true});
            skFitSpline(sketch, "E17", {"points": [v(-35.84, 46) * mm, v(-35.66, 46.26) * mm, v(-35.58, 46.43) * mm, v(-35.43, 46.74) * mm, v(-35.1, 47.27) * mm, v(-34.87, 47.6) * mm, v(-34.64, 47.93) * mm, v(-34.5, 48.2) * mm, v(-34.25, 48.52) * mm, v(-34.05, 48.72) * mm, v(-33.85, 48.95) * mm, v(-33.72, 49.06) * mm, v(-33.77, 49.16) * mm, v(-33.89, 49.3) * mm, v(-34.05, 49.48) * mm, v(-34.16, 49.5) * mm, v(-34.26, 49.48) * mm, v(-34.46, 49.42) * mm, v(-34.49, 49.55) * mm, v(-34.4, 49.68) * mm, v(-34.21, 49.93) * mm, v(-34.12, 50.04) * mm, v(-34.01, 50.19) * mm, v(-33.93, 49.98) * mm, v(-33.8, 49.93) * mm, v(-33.7, 50) * mm, v(-33.6, 50) * mm, v(-33.6, 49.94) * mm, v(-33.47, 49.9) * mm, v(-33.41, 49.8) * mm, v(-33.35, 49.8) * mm, v(-33.18, 50.02) * mm, v(-33.05, 50.2) * mm, v(-32.97, 50.3) * mm, v(-32.86, 50.44) * mm, v(-32.73, 50.63) * mm, v(-32.66, 50.79) * mm, v(-32.56, 50.93) * mm, v(-32.38, 51.12) * mm, v(-32.29, 51.33) * mm, v(-32.25, 51.42) * mm, v(-32.18, 51.52) * mm, v(-32.11, 51.67) * mm, v(-32, 51.78) * mm, v(-31.98, 51.95) * mm, v(-31.9, 52.06) * mm, v(-31.79, 52.17) * mm, v(-31.68, 52.33) * mm, v(-31.54, 52.56) * mm, v(-31.42, 52.72) * mm, v(-31.31, 52.8) * mm, v(-31.2, 52.68) * mm, v(-31.13, 52.54) * mm, v(-31.06, 52.35) * mm, v(-30.97, 52.2) * mm, v(-30.9, 52.11) * mm, v(-30.83, 52) * mm, v(-30.75, 51.88) * mm, v(-30.63, 51.7) * mm, v(-30.5, 51.48) * mm, v(-30.41, 51.3) * mm, v(-30.33, 51.15) * mm, v(-30.3, 50.99) * mm, v(-30.28, 50.81) * mm, v(-30.26, 50.63) * mm, v(-30.2, 50.48) * mm, v(-30.22, 50.4) * mm, v(-30.31, 50.48) * mm, v(-30.38, 50.6) * mm, v(-30.44, 50.76) * mm, v(-30.5, 50.84) * mm, v(-30.56, 50.97) * mm, v(-30.62, 51.02) * mm, v(-30.76, 51.13) * mm, v(-30.8, 51.19) * mm, v(-30.72, 51.2) * mm, v(-30.71, 51.27) * mm, v(-30.8, 51.3) * mm, v(-30.9, 51.34) * mm, v(-30.88, 51.4) * mm, v(-30.84, 51.46) * mm, v(-30.9, 51.51) * mm, v(-30.95, 51.47) * mm, v(-31.04, 51.59) * mm, v(-31.05, 51.66) * mm, v(-31.14, 51.7) * mm, v(-31.27, 51.84) * mm, v(-31.3, 51.7) * mm, v(-31.4, 51.52) * mm, v(-31.43, 51.38) * mm, v(-31.54, 51.28) * mm, v(-31.7, 51.43) * mm, v(-31.73, 51.28) * mm, v(-31.77, 51.08) * mm, v(-31.77, 51) * mm, v(-31.85, 50.91) * mm, v(-31.8, 50.78) * mm, v(-31.81, 50.67) * mm, v(-31.95, 50.69) * mm, v(-32.04, 50.65) * mm, v(-32.07, 50.49) * mm, v(-32.16, 50.3) * mm, v(-32.3, 50.08) * mm, v(-32.4, 49.93) * mm, v(-32.48, 49.83) * mm, v(-32.64, 49.59) * mm, v(-32.84, 49.3) * mm, v(-33.03, 49) * mm, v(-33.18, 48.78) * mm, v(-33.43, 48.47) * mm, v(-33.57, 48.33) * mm, v(-33.67, 48.18) * mm, v(-33.73, 48.02) * mm, v(-33.87, 47.83) * mm, v(-34, 47.72) * mm, v(-33.97, 47.63) * mm, v(-34.12, 47.44) * mm, v(-34.31, 47.16) * mm, v(-34.5, 46.88) * mm, v(-34.66, 46.62) * mm, v(-34.57, 46.57) * mm, v(-34.38, 46.62) * mm, v(-34.28, 46.53) * mm, v(-34.17, 46.45) * mm, v(-33.98, 46.52) * mm, v(-33.76, 46.56) * mm, v(-33.66, 46.52) * mm, v(-33.42, 46.77) * mm, v(-33.4, 46.7) * mm, v(-33.32, 46.63) * mm, v(-33.27, 46.76) * mm, v(-33.15, 46.73) * mm, v(-33.19, 46.58) * mm, v(-33.04, 46.5) * mm, v(-32.8, 46.42) * mm, v(-32.6, 46.35) * mm, v(-32.25, 46.32) * mm, v(-31.91, 46.37) * mm, v(-31.6, 46.44) * mm, v(-31.4, 46.5) * mm, v(-31.3, 46.58) * mm, v(-31.08, 46.62) * mm, v(-30.98, 46.48) * mm, v(-30.76, 46.5) * mm, v(-30.52, 46.54) * mm, v(-30.21, 46.66) * mm, v(-30.2, 46.58) * mm, v(-30.01, 46.56) * mm, v(-29.83, 46.72) * mm, v(-29.68, 46.62) * mm, v(-29.1, 46.76) * mm, v(-28.97, 46.67) * mm, v(-29.06, 46.65) * mm, v(-28.93, 46.53) * mm, v(-28.63, 46.6) * mm, v(-28.76, 46.84) * mm, v(-28.93, 47.07) * mm, v(-29.05, 47.27) * mm, v(-29.07, 47.43) * mm, v(-29.18, 47.51) * mm, v(-29.37, 47.74) * mm, v(-29.18, 47.75) * mm, v(-29.42, 47.94) * mm, v(-29.6, 48.08) * mm, v(-29.8, 48.29) * mm, v(-29.93, 48.4) * mm, v(-30.03, 48.47) * mm, v(-29.98, 48.55) * mm, v(-30.1, 48.64) * mm, v(-30.33, 48.77) * mm, v(-30.37, 48.94) * mm, v(-30.66, 49.13) * mm, v(-30.91, 49.25) * mm, v(-31.18, 49.42) * mm, v(-31.37, 49.49) * mm, v(-31.76, 49.5) * mm, v(-32.05, 49.23) * mm, v(-32.22, 48.92) * mm, v(-32.25, 48.67) * mm, v(-32.44, 48.45) * mm, v(-32.43, 48.3) * mm, v(-32.5, 48.2) * mm, v(-32.41, 47.92) * mm, v(-32.3, 47.68) * mm, v(-31.96, 47.72) * mm, v(-31.63, 47.68) * mm, v(-31.38, 47.66) * mm, v(-31.21, 47.71) * mm, v(-30.94, 47.65) * mm, v(-30.71, 47.76) * mm, v(-30.48, 47.7) * mm, v(-30.47, 47.53) * mm, v(-30.35, 47.58) * mm, v(-30.41, 47.8) * mm, v(-30.37, 47.9) * mm, v(-30.5, 48.07) * mm, v(-30.61, 48.25) * mm, v(-30.82, 48.3) * mm, v(-30.76, 48.43) * mm, v(-30.62, 48.45) * mm, v(-30.47, 48.44) * mm, v(-30.3, 48.3) * mm, v(-30.15, 48.06) * mm, v(-30.06, 47.84) * mm, v(-30.19, 47.7) * mm, v(-30.2, 47.54) * mm, v(-30.37, 47.42) * mm, v(-30.59, 47.41) * mm, v(-30.77, 47.4) * mm, v(-31.06, 47.4) * mm, v(-31.17, 47.4) * mm, v(-31.25, 47.5) * mm, v(-31.38, 47.4) * mm, v(-31.5, 47.4) * mm, v(-31.68, 47.36) * mm, v(-31.94, 47.43) * mm, v(-32.12, 47.34) * mm, v(-32.37, 47.3) * mm, v(-32.62, 47.33) * mm, v(-32.77, 47.38) * mm, v(-33, 47.47) * mm, v(-33.05, 47.64) * mm, v(-33, 47.97) * mm, v(-32.92, 48.22) * mm, v(-32.87, 48.41) * mm, v(-32.84, 48.7) * mm, v(-32.74, 48.73) * mm, v(-32.82, 48.85) * mm, v(-32.8, 49.01) * mm, v(-32.67, 49.22) * mm, v(-32.48, 49.38) * mm, v(-32.29, 49.69) * mm, v(-32.08, 49.96) * mm, v(-31.82, 50.03) * mm, v(-31.73, 49.92) * mm, v(-31.64, 49.98) * mm, v(-31.45, 50.04) * mm, v(-31.22, 50) * mm, v(-31.15, 49.92) * mm, v(-30.96, 49.97) * mm, v(-30.69, 49.87) * mm, v(-30.6, 49.95) * mm, v(-30.44, 49.9) * mm, v(-30.34, 49.72) * mm, v(-30.19, 49.57) * mm, v(-30.01, 49.46) * mm, v(-29.95, 49.37) * mm, v(-29.79, 49.16) * mm, v(-29.53, 49.06) * mm, v(-29.34, 49.02) * mm, v(-29.24, 48.84) * mm, v(-29.1, 48.7) * mm, v(-29.14, 48.62) * mm, v(-29, 48.54) * mm, v(-28.9, 48.43) * mm, v(-28.74, 48.28) * mm, v(-28.87, 48.24) * mm, v(-28.78, 48.12) * mm, v(-28.58, 48.05) * mm, v(-28.49, 47.88) * mm, v(-28.3, 47.6) * mm, v(-27.98, 47.17) * mm, v(-27.81, 46.91) * mm, v(-27.49, 46.37) * mm, v(-27.15, 45.87) * mm, v(-27.19, 45.82) * mm, v(-27.42, 45.84) * mm, v(-27.77, 45.82) * mm, v(-28.2, 45.8) * mm, v(-28.7, 45.8) * mm, v(-29.21, 45.82) * mm, v(-29.74, 45.81) * mm, v(-30.1, 45.81) * mm, v(-30.64, 45.82) * mm, v(-31.2, 45.83) * mm, v(-31.21, 45.74) * mm, v(-31.14, 45.66) * mm, v(-31.02, 45.6) * mm, v(-31.01, 45.43) * mm, v(-30.87, 45.5) * mm, v(-30.85, 45.36) * mm, v(-30.79, 45.21) * mm, v(-30.59, 45.25) * mm, v(-30.68, 45.04) * mm, v(-30.54, 44.98) * mm, v(-30.42, 45.1) * mm, v(-30.36, 44.9) * mm, v(-30.18, 45.06) * mm, v(-29.98, 45) * mm, v(-29.95, 44.84) * mm, v(-29.98, 44.66) * mm, v(-30.07, 44.42) * mm, v(-30.29, 44.31) * mm, v(-30.47, 44.35) * mm, v(-30.64, 44.42) * mm, v(-30.81, 44.5) * mm, v(-31.02, 44.56) * mm, v(-31.22, 44.63) * mm, v(-31.28, 44.77) * mm, v(-31.42, 44.85) * mm, v(-31.47, 45.04) * mm, v(-31.6, 45.08) * mm, v(-31.62, 45.41) * mm, v(-31.8, 45.5) * mm, v(-31.86, 45.61) * mm, v(-31.85, 45.78) * mm, v(-31.83, 45.87) * mm, v(-32, 45.89) * mm, v(-32.18, 45.87) * mm, v(-32.47, 45.88) * mm, v(-32.69, 45.92) * mm, v(-32.9, 45.9) * mm, v(-33.03, 45.85) * mm, v(-33.31, 45.84) * mm, v(-33.75, 45.8) * mm, v(-34.18, 45.82) * mm, v(-34.53, 45.86) * mm, v(-34.98, 45.91) * mm, v(-35.34, 45.96) * mm, v(-35.5, 45.9) * mm, v(-35.72, 45.9) * mm, v(-35.84, 46) * mm]});
            skFitSpline(sketch, "E18", {"points": [v(-29.1, 49.65) * mm, v(-29.06, 49.78) * mm, v(-28.95, 49.85) * mm, v(-28.95, 49.96) * mm, v(-28.88, 49.98) * mm, v(-28.8, 49.97) * mm, v(-28.78, 50.13) * mm, v(-28.67, 50.03) * mm, v(-28.62, 50.14) * mm, v(-28.66, 50.18) * mm, v(-28.55, 50.2) * mm, v(-28.47, 50.29) * mm, v(-28.49, 50.45) * mm, v(-28.39, 50.32) * mm, v(-28.28, 50.33) * mm, v(-28.28, 50.16) * mm, v(-28.2, 50.05) * mm, v(-28.18, 49.86) * mm, v(-28.26, 49.71) * mm, v(-28.19, 49.57) * mm, v(-28.32, 49.63) * mm, v(-28.39, 49.55) * mm, v(-28.29, 49.4) * mm, v(-28.55, 49.44) * mm, v(-28.6, 49.31) * mm, v(-29.1, 49.65) * mm]});
            skFitSpline(sketch, "E19", {"points": [v(-30.72, 48.57) * mm, v(-30.8, 48.69) * mm, v(-30.98, 48.65) * mm, v(-30.88, 48.58) * mm, v(-30.72, 48.57) * mm]});
            skFitSpline(sketch, "E20", {"points": [v(-30.92, 48.47) * mm, v(-31.04, 48.52) * mm, v(-31.03, 48.43) * mm, v(-30.92, 48.36) * mm, v(-30.92, 48.47) * mm]});
            skFitSpline(sketch, "E21", {"points": [v(-31.18, 48.68) * mm, v(-31.32, 48.7) * mm, v(-31.3, 48.58) * mm, v(-31.2, 48.56) * mm, v(-31.2, 48.49) * mm, v(-31.1, 48.45) * mm, v(-31.1, 48.54) * mm, v(-31.15, 48.6) * mm, v(-31.18, 48.68) * mm]});
            skFitSpline(sketch, "E22", {"points": [v(-31.5, 48.73) * mm, v(-31.5, 48.61) * mm, v(-31.4, 48.61) * mm, v(-31.4, 48.7) * mm, v(-31.5, 48.73) * mm]});
            skFitSpline(sketch, "E23", {"points": [v(-32.5, 46.5) * mm, v(-32.3, 46.51) * mm, v(-32.26, 46.6) * mm, v(-32.13, 46.65) * mm, v(-32.06, 46.69) * mm, v(-32, 46.6) * mm, v(-31.85, 46.7) * mm, v(-31.65, 46.68) * mm, v(-31.5, 46.65) * mm, v(-31.59, 46.57) * mm, v(-31.77, 46.53) * mm, v(-31.94, 46.49) * mm, v(-32.02, 46.43) * mm, v(-32.1, 46.5) * mm, v(-32.2, 46.47) * mm, v(-32.24, 46.4) * mm, v(-32.5, 46.42) * mm, v(-32.5, 46.5) * mm]});
            skFitSpline(sketch, "E24", {"points": [v(-33.07, 46.76) * mm, v(-33.06, 46.6) * mm, v(-32.93, 46.63) * mm, v(-32.87, 46.7) * mm, v(-32.86, 46.75) * mm, v(-33.07, 46.76) * mm]});
            skFitSpline(sketch, "E25", {"points": [v(-30.85, 46.6) * mm, v(-30.8, 46.73) * mm, v(-30.69, 46.7) * mm, v(-30.8, 46.57) * mm, v(-30.85, 46.6) * mm]});
            skFitSpline(sketch, "E26", {"points": [v(-28.83, 46.76) * mm, v(-28.91, 46.75) * mm, v(-28.9, 46.66) * mm, v(-28.86, 46.58) * mm, v(-28.79, 46.62) * mm, v(-28.83, 46.76) * mm]});
            skFitSpline(sketch, "E27", {"points": [v(-31.71, 50.16) * mm, v(-31.43, 50.22) * mm, v(-31.26, 50.18) * mm, v(-31.13, 50.2) * mm, v(-31.08, 50.26) * mm, v(-30.78, 50.12) * mm, v(-30.96, 50.1) * mm, v(-31.06, 50.04) * mm, v(-31.26, 50.08) * mm, v(-31.48, 50.09) * mm, v(-31.67, 50.04) * mm, v(-31.8, 50.07) * mm, v(-31.71, 50.16) * mm]});
            skLineSegment(sketch, "E28", {"start": v(-31.31, 53.87) * mm, "end": v(-31.43, 43.8) * mm, "construction": true});
            skSolve(sketch);
        }
        {
            var Q0;
            Q0 = qSketchRegion(id + "F4", true);
            var Q1;
            Q1=makeQuery(id+"F4.imprint","IMPRINT",FACE,{"disambiguationData":[TD([[makeQuery(id+"F4.imprint","IMPRINT",EDGE,{"derivedFrom":sQuery(id+"F4.wireOp",EDGE,"E5")}),1.0]])]});
            extrude(context, id + "F5", {"entities" : qUnion([Q0, Q1]), "depth" : 1.27 * mm, "offsetDistance" : 25.4 * mm});
        }
    });
